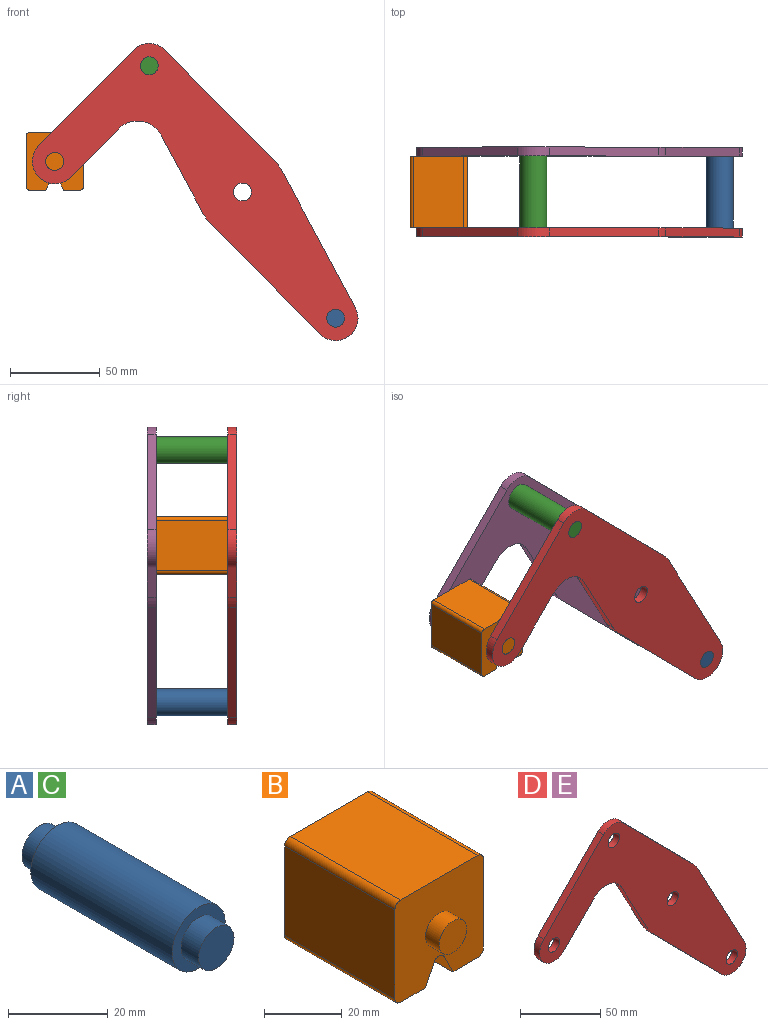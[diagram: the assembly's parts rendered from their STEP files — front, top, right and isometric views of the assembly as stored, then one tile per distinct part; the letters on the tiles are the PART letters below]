
ASSEMBLY  parts=5 mates=3
PART A: 7 faces, bbox 15x50x15 mm
  f0: cylinder r=7.5mm len=40mm, axis (0,-1,0), area 1885mm2, adj f2,f5
  f1: cylinder r=5mm len=10mm, axis (0,1,0), area 157.1mm2, adj f2,f3
  f2: plane 15x15mm, normal (0,-1,0), area 98.2mm2, adj f0,f1
  f3: plane 10x10mm, normal (0,-1,0), area 78.5mm2, adj f1
  f4: cylinder r=5mm len=10mm, axis (0,-1,0), area 157.1mm2, adj f5,f6
  f5: plane 15x15mm, normal (0,1,0), area 98.2mm2, adj f0,f4
  f6: plane 10x10mm, normal (0,1,0), area 78.5mm2, adj f4
PART B: 18 faces, bbox 32.1x50x32.1 mm
  f0: plane 40x28.08mm, normal (1,0,0), area 1123.1mm2, adj f4,f10,f13,f14
  f1: plane 40x9.04mm, normal (0,0,-1), area 361.6mm2, adj f2,f4,f10,f14
  f2: plane 40x6.42mm, normal (-0.89,0,-0.45), area 287.2mm2, adj f1,f4,f10,f15
  f3: plane 40x6.42mm, normal (0.89,0,-0.45), area 287.2mm2, adj f4,f5,f10,f15
  f4: plane 32.08x32.08mm, normal (0,-1,0), area 900.6mm2, adj f0,f1,f2,f3,f5,f6,f7,f9
  f5: plane 40x9.04mm, normal (0,0,-1), area 361.6mm2, adj f3,f4,f10,f16
  f6: plane 40x28.08mm, normal (0,0,1), area 1123.1mm2, adj f4,f10,f13,f17
  f7: plane 40x28.08mm, normal (-1,0,0), area 1123.1mm2, adj f4,f10,f16,f17
  f8: plane 10x10mm, normal (0,-1,0), area 78.5mm2, adj f9
  f9: cylinder r=5mm len=10mm, axis (0,1,0), area 157.1mm2, adj f4,f8
  f10: plane 32.08x32.08mm, normal (0,1,0), area 900.6mm2, adj f0,f1,f2,f3,f5,f6,f7,f12
  f11: plane 10x10mm, normal (0,1,0), area 78.5mm2, adj f12
  f12: cylinder r=5mm len=10mm, axis (0,-1,0), area 157.1mm2, adj f10,f11
  f13: cylinder r=2mm len=40mm, axis (0,1,0), area 125.7mm2, adj f0,f4,f6,f10
  f14: cylinder r=2mm len=40mm, axis (0,-1,0), area 125.7mm2, adj f0,f1,f4,f10
  f15: cylinder r=2mm len=40mm, axis (0,1,0), area 177.1mm2, adj f2,f3,f4,f10
  f16: cylinder r=2mm len=40mm, axis (0,1,0), area 125.7mm2, adj f4,f5,f7,f10
  f17: cylinder r=2mm len=40mm, axis (0,-1,0), area 125.7mm2, adj f4,f6,f7,f10
PART C: same geometry as A
PART D: 18 faces, bbox 181.7x5x165.8 mm
  f0: plane 43.49x23.35mm, normal (-0.88,0,-0.47), area 246.8mm2, adj f1,f14,f16,f17
  f1: cylinder r=25mm len=5.75mm, axis (0,1,0), area 35.8mm2, adj f0,f2,f16,f17
  f2: plane 61.6x60.87mm, normal (-0.71,0,-0.7), area 433mm2, adj f1,f3,f16,f17
  f3: cylinder r=12.5mm len=21.39mm, axis (0,1,0), area 178.4mm2, adj f2,f4,f16,f17
  f4: plane 76.3x40.96mm, normal (0.88,0,0.47), area 433mm2, adj f3,f5,f16,f17
  f5: cylinder r=25mm len=5.75mm, axis (0,1,0), area 35.8mm2, adj f4,f6,f16,f17
  f6: plane 61.6x60.87mm, normal (0.71,0,0.7), area 433mm2, adj f5,f7,f16,f17
  f7: cylinder r=12.5mm len=17.78mm, axis (0,1,0), area 98.9mm2, adj f6,f8,f16,f17
  f8: plane 53.35x52.71mm, normal (-0.71,0,0.7), area 375mm2, adj f7,f9,f16,f17
  f9: cylinder r=12.5mm len=21.39mm, axis (0,1,0), area 196.3mm2, adj f8,f10,f16,f17
  f10: plane 26.86x26.54mm, normal (0.71,0,-0.7), area 188.8mm2, adj f9,f14,f16,f17
  f11: cylinder r=5mm len=10mm, axis (0,1,0), area 157.1mm2, adj f16,f17
  f12: cylinder r=5mm len=10mm, axis (0,1,0), area 157.1mm2, adj f16,f17
  f13: cylinder r=5mm len=10mm, axis (0,1,0), area 157.1mm2, adj f16,f17
  f14: cylinder r=15mm len=23.89mm, axis (0,1,0), area 140.2mm2, adj f0,f10,f16,f17
  f15: cylinder r=5mm len=10mm, axis (0,1,0), area 157.1mm2, adj f16,f17
  f16: plane 181.66x165.78mm, normal (0,-1,0), area 8710.1mm2, adj f0,f1,f2,f3,f4,f5,f6,f7
  f17: plane 181.66x165.78mm, normal (0,1,0), area 8710.1mm2, adj f0,f1,f2,f3,f4,f5,f6,f7
PART E: same geometry as D
PLACE A t=(103.95,-20,-140.78)mm
PLACE B t=(0,-20,0)mm
PLACE C t=(0,-20,0)mm
PLACE D t=(0,-20,0)mm fixed
PLACE E t=(0,25,0)mm
MATE revolute B.f9 <-> D.f9  axis (0,1,0) through (-104.69,-20,17.04)mm
MATE fastened C.f0 <-> E.f7  axis (0,-1,0) through (-51.98,20,70.39)mm
MATE fastened A.f0 <-> D.f3  axis (0,1,0) through (51.98,-20,-70.39)mm
